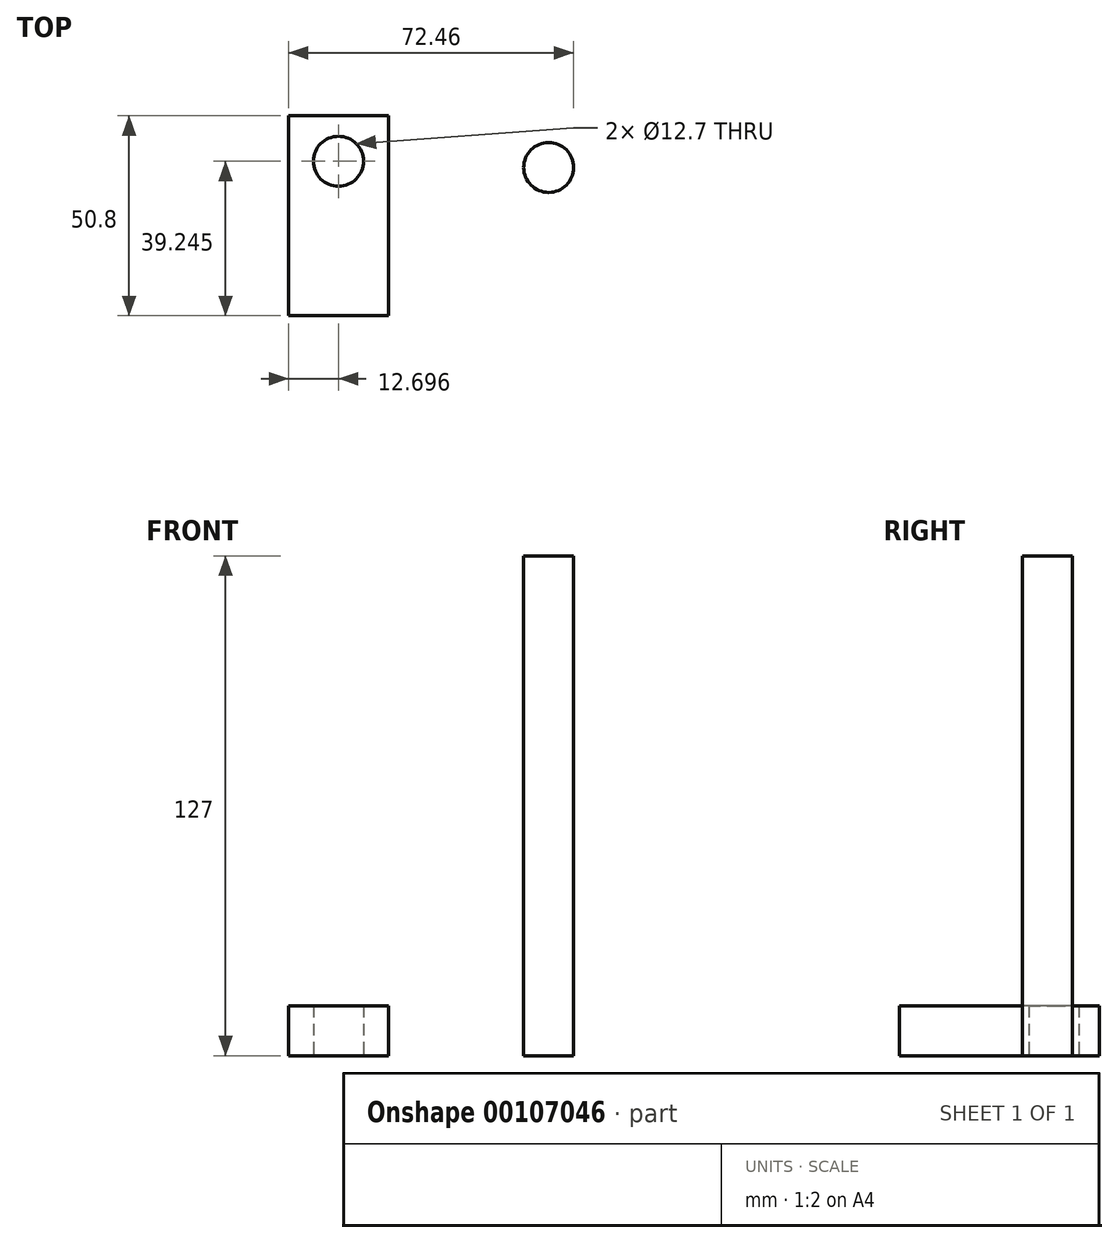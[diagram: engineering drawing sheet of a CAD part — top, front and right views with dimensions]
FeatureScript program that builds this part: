
annotation { "Feature Type Name" : "Feature", "Feature Type Description" : "" }
export const myFeature = defineFeature(function(context is Context, id is Id, definition is map)
    precondition{}
    {
        {
            var Q0;
            Q0=qCreatedBy(makeId("Top.planeOp"),FACE);
            var sketch = newSketch(context, id + "F0", { "sketchPlane" : qUnion([Q0])});
            skLineSegment(sketch, "E0.bottom", {"start": v(-52.02, 40.24) * mm, "end": v(-26.62, 40.24) * mm});
            skLineSegment(sketch, "E0.top", {"start": v(-52.02, -10.56) * mm, "end": v(-26.62, -10.56) * mm});
            skLineSegment(sketch, "E0.left", {"start": v(-52.02, 40.24) * mm, "end": v(-52.02, -10.56) * mm});
            skLineSegment(sketch, "E0.right", {"start": v(-26.62, 40.24) * mm, "end": v(-26.62, -10.56) * mm});
            skPoint(sketch, "E1.middle.positionSnap0", {"position": v(-39.32, 40.24) * mm});
            skPoint(sketch, "E1.centerSnap0", {"position": v(-39.32, 40.24) * mm});
            skCircle(sketch, "E2", {"center": v(-39.32, 28.68) * mm, "radius": 6.35 * mm});
            skSolve(sketch);
        }
        {
            var Q0;
            Q0=makeQuery(id+"F0.imprint","IMPRINT",FACE,{"disambiguationData":[TD([[makeQuery(id+"F0.imprint","IMPRINT",EDGE,{"derivedFrom":sQuery(id+"F0.wireOp",EDGE,"E0.bottom")}),-1.0]])]});
            extrude(context, id + "F1", {"entities" : qUnion([Q0]), "depth" : 12.7 * mm});
        }
        {
            var Q0;
            Q0=qCreatedBy(makeId("Top.planeOp"),FACE);
            var sketch = newSketch(context, id + "F2", { "sketchPlane" : qUnion([Q0])});
            skCircle(sketch, "E3", {"center": v(14.09, 27.1) * mm, "radius": 6.35 * mm});
            skSolve(sketch);
        }
        {
            var Q0;
            Q0=makeQuery(id+"F2.imprint","IMPRINT",FACE,{"disambiguationData":[TD([[makeQuery(id+"F2.imprint","IMPRINT",EDGE,{"derivedFrom":sQuery(id+"F2.wireOp",EDGE,"E3")}),1.0]])]});
            extrude(context, id + "F3", {"entities" : qUnion([Q0]), "depth" : 127 * mm});
        }
    });
